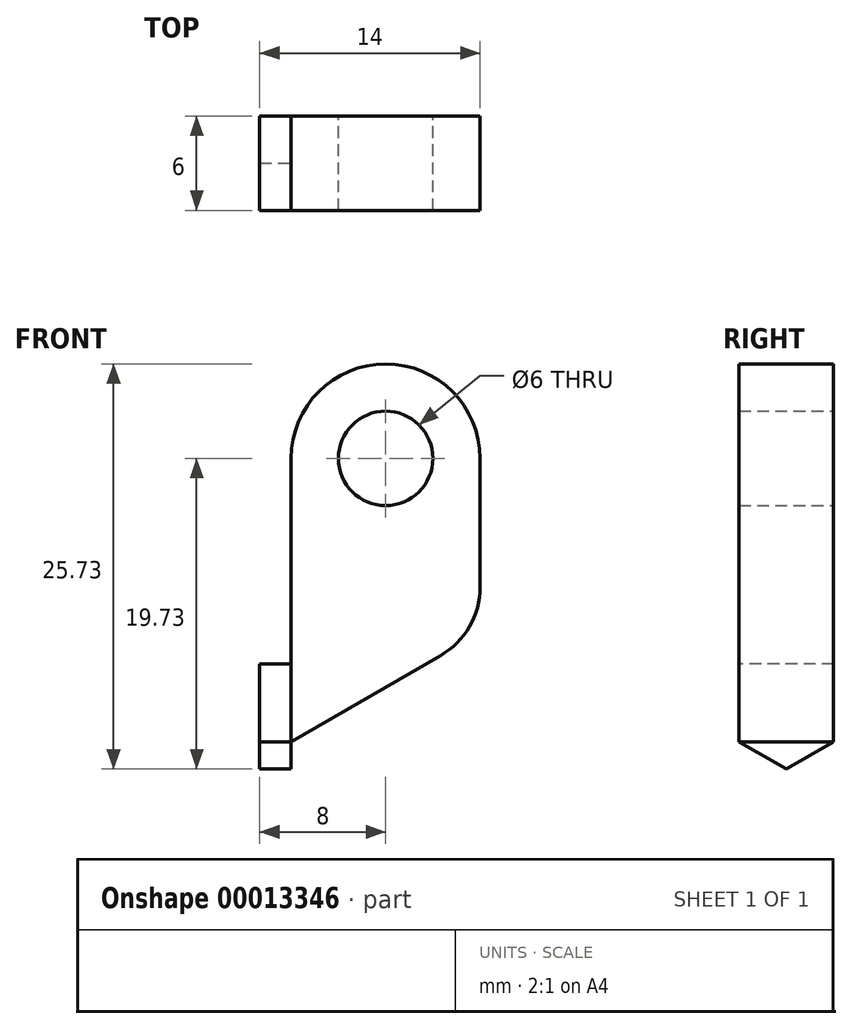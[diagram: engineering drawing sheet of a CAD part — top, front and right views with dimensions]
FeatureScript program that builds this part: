
annotation { "Feature Type Name" : "Feature", "Feature Type Description" : "" }
export const myFeature = defineFeature(function(context is Context, id is Id, definition is map)
    precondition{}
    {
        {
            var Q0;
            Q0=qCreatedBy(makeId("Front.planeOp"),FACE);
            var sketch = newSketch(context, id + "F0", { "sketchPlane" : qUnion([Q0])});
            skCircle(sketch, "E0", {"center": v(0, 0) * mm, "radius": 3 * mm});
            skArc(sketch, "E1", {"start": v(6, 0) * mm, "mid": v(0, 6) * mm, "end": v(-6, 0) * mm});
            skLineSegment(sketch, "E2", {"start": v(-6, 0) * mm, "end": v(6, 0) * mm, "construction": true});
            skLineSegment(sketch, "E3", {"start": v(-6, 0) * mm, "end": v(-6, -18) * mm});
            skLineSegment(sketch, "E4", {"start": v(6, 0) * mm, "end": v(6, -11.07) * mm});
            skLineSegment(sketch, "E5", {"start": v(6, -11.07) * mm, "end": v(-6, -18) * mm});
            skSolve(sketch);
        }
        {
            var Q0;
            Q0=makeQuery(id+"F0.imprint","IMPRINT",FACE,{"disambiguationData":[TD([[makeQuery(id+"F0.imprint","IMPRINT",EDGE,{"derivedFrom":sQuery(id+"F0.wireOp",EDGE,"E0")}),-1.0]])]});
            extrude(context, id + "F1", {"entities" : qUnion([Q0]), "depth" : 6 * mm});
        }
        {
            var Q0;
            Q0=makeQuery(id+"F1.opExtrude","SWEPT_EDGE",EDGE,{"disambiguationData":[OSD([sQuery(id+"F0.wireOp",EDGE,"E4"),sQuery(id+"F0.wireOp",EDGE,"E5")])]});
            fillet(context, id + "F2", {"entities" : qUnion([Q0]), "radius" : 5 * mm, "tangentPropagation" : true, "allowEdgeOverflow" : false});
        }
        {
            var Q0;
            Q0=makeQuery(id+"F1.opExtrude","SWEPT_FACE",FACE,{"disambiguationData":[OSD([sQuery(id+"F0.wireOp",EDGE,"E3")])]});
            var sketch = newSketch(context, id + "F3", { "sketchPlane" : qUnion([Q0])});
            skLineSegment(sketch, "E6.bottom", {"start": v(0, -13.05) * mm, "end": v(6, -13.05) * mm});
            skLineSegment(sketch, "E6.left", {"start": v(0, -13.05) * mm, "end": v(0, -18) * mm});
            skLineSegment(sketch, "E6.right", {"start": v(6, -13.05) * mm, "end": v(6, -18) * mm});
            skLineSegment(sketch, "E7", {"start": v(0, -18) * mm, "end": v(3, -19.73) * mm});
            skPoint(sketch, "E8.0.start.orphan", {"position": v(0, -22.83) * mm});
            skLineSegment(sketch, "E9", {"start": v(3, -19.73) * mm, "end": v(3, 7.78) * mm, "construction": true});
            skPoint(sketch, "E10.orphan", {"position": v(3, -18) * mm});
            skLineSegment(sketch, "E11", {"start": v(6, -18) * mm, "end": v(3, -19.73) * mm});
            skSolve(sketch);
        }
        {
            var Q0;
            {var subQ4=sQuery(id+"F3.wireOp",EDGE,"E6.bottom");Q0=makeQuery(id+"F3.imprint","IMPRINT",FACE,{"disambiguationData":[TD([[makeQuery(id+"F3.imprint","IMPRINT",EDGE,{"derivedFrom":subQ4}),-1.0]])]});}
            var Q1;
            {var subQ3=sQuery(id+"F3.wireOp",EDGE,"E7");Q1=makeQuery(id+"F3.imprint","IMPRINT",FACE,{"disambiguationData":[TD([[makeQuery(id+"F3.imprint","IMPRINT",EDGE,{"derivedFrom":subQ3}),1.0]])]});}
            extrude(context, id + "F4", {"entities" : qUnion([Q0, Q1]), "depth" : 3 * mm});
        }
        {
            var Q0;
            Q0=makeQuery(id+"F4.opExtrude","SWEPT_BODY",BODY,{"disambiguationData":[OSD([sQuery(id+"F3.wireOp",EDGE,"E6.bottom"),sQuery(id+"F3.wireOp",EDGE,"E6.left"),sQuery(id+"F3.wireOp",EDGE,"E6.right"),sQuery(id+"F3.wireOp",EDGE,"E7"),sQuery(id+"F3.wireOp",EDGE,"775d553f-8be8-4dc3-a27b-2b76646dee19")])]});
            deleteBodies(context, id + "F5", {"entities" : qUnion([Q0])});
        }
        {
            var Q0;
            Q0=makeQuery(id+"F3.imprint","IMPRINT",FACE,{"disambiguationData":[TD([[makeQuery(id+"F3.imprint","IMPRINT",EDGE,{"derivedFrom":sQuery(id+"F3.wireOp",EDGE,"E7")}),1.0]])]});
            var Q1;
            Q1=makeQuery(id+"F3.imprint","IMPRINT",FACE,{"disambiguationData":[TD([[makeQuery(id+"F3.imprint","IMPRINT",EDGE,{"derivedFrom":sQuery(id+"F3.wireOp",EDGE,"E6.bottom")}),-1.0]])]});
            extrude(context, id + "F6", {"entities" : qUnion([Q0, Q1]), "depth" : 2 * mm});
        }
    });
